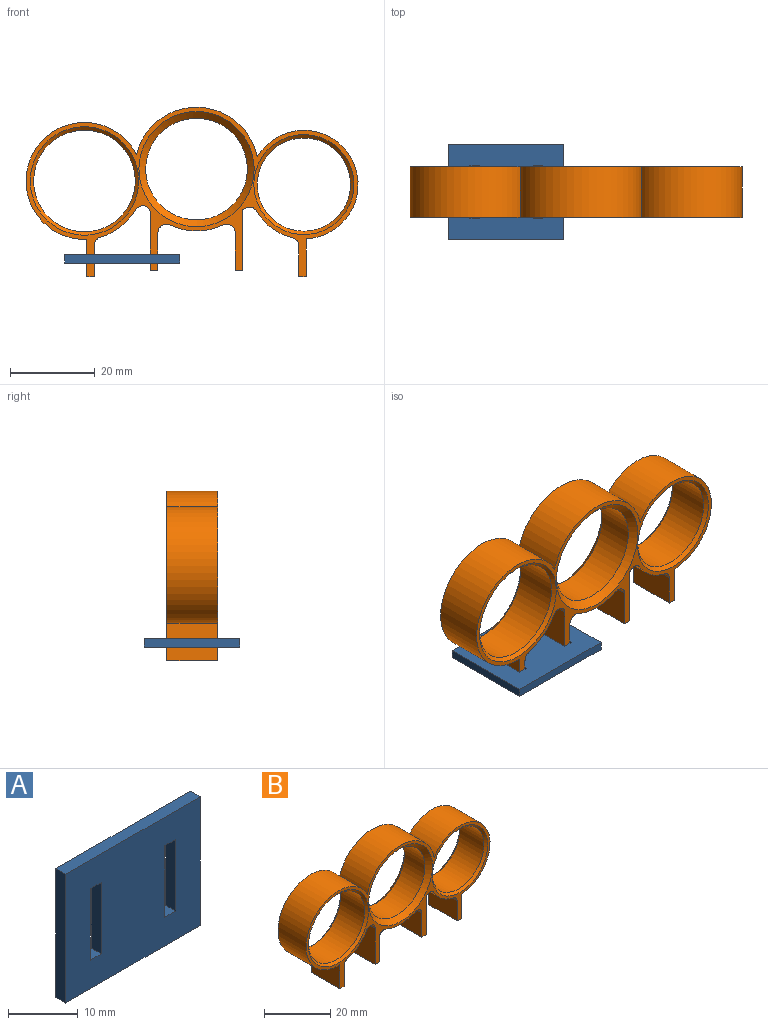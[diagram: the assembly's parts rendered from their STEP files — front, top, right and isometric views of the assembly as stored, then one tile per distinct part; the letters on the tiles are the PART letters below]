
ASSEMBLY  parts=2 mates=1
PART A: 14 faces, bbox 27.2x2x22.5 mm
  f0: plane 27.2x2mm, normal (0,0,1), area 54.4mm2, adj f1,f11,f12,f13
  f1: plane 22.5x2mm, normal (-1,0,0), area 45mm2, adj f0,f2,f12,f13
  f2: plane 27.2x2mm, normal (0,0,-1), area 54.4mm2, adj f1,f11,f12,f13
  f3: plane 12.5x2mm, normal (1,0,0), area 25mm2, adj f4,f9,f12,f13
  f4: plane 2.2x2mm, normal (0,0,-1), area 4.4mm2, adj f3,f5,f12,f13
  f5: plane 12.5x2mm, normal (-1,0,0), area 25mm2, adj f4,f9,f12,f13
  f6: plane 2.2x2mm, normal (0,0,-1), area 4.4mm2, adj f7,f10,f12,f13
  f7: plane 12.5x2mm, normal (-1,0,0), area 25mm2, adj f6,f8,f12,f13
  f8: plane 2.2x2mm, normal (0,0,1), area 4.4mm2, adj f7,f10,f12,f13
  f9: plane 2.2x2mm, normal (0,0,1), area 4.4mm2, adj f3,f5,f12,f13
  f10: plane 12.5x2mm, normal (1,0,0), area 25mm2, adj f6,f8,f12,f13
  f11: plane 22.5x2mm, normal (1,0,0), area 45mm2, adj f0,f2,f12,f13
  f12: plane 27.2x22.5mm, normal (0,-1,0), area 557mm2, adj f0,f1,f2,f3,f4,f5,f6,f7
  f13: plane 27.2x22.5mm, normal (0,1,0), area 557mm2, adj f0,f1,f2,f3,f4,f5,f6,f7
PART B: 37 faces, bbox 78.4x12x40 mm
  f0: cylinder r=12.8mm len=25.59mm, axis (0,1,0), area 635.2mm2, adj f4,f10,f11,f21
  f1: cylinder r=14.6mm len=12.49mm, axis (0,1,0), area 154.9mm2, adj f10,f11,f24,f25
  f2: cylinder r=14.6mm len=12mm, axis (0,1,0), area 1.2mm2, adj f10,f11,f20,f30
  f3: cylinder r=13.8mm len=27.6mm, axis (0,1,0), area 708.5mm2, adj f4,f10,f11,f12
  f4: cylinder r=14.6mm len=28.49mm, axis (0,1,0), area 473.4mm2, adj f0,f3,f10,f11
  f5: cylinder r=13.8mm len=12mm, axis (0,1,0), area 127.9mm2, adj f10,f11,f27,f29
  f6: cylinder r=12mm len=24mm, axis (0,1,0), area 784.1mm2, adj f33,f36
  f7: cylinder r=12mm len=24mm, axis (0,1,0), area 663.5mm2, adj f31,f32
  f8: cylinder r=11mm len=22mm, axis (0,1,0), area 718.8mm2, adj f34,f35
  f9: cylinder r=12.8mm len=12mm, axis (0,1,0), area 128mm2, adj f10,f11,f26,f30
  f10: plane 78.39x40mm, normal (0,-1,0), area 317.2mm2, adj f0,f1,f2,f3,f4,f5,f9,f12
  f11: plane 78.39x40mm, normal (0,1,0), area 317.2mm2, adj f0,f1,f2,f3,f4,f5,f9,f12
  f12: plane 12x8.81mm, normal (-1,0,0), area 105.7mm2, adj f3,f10,f11,f13
  f13: plane 12x1.8mm, normal (0,0,-1), area 21.6mm2, adj f10,f11,f12,f14
  f14: plane 12x7.41mm, normal (1,0,0), area 88.9mm2, adj f10,f11,f13,f29
  f15: plane 12x8.89mm, normal (1,0,0), area 106.7mm2, adj f10,f11,f17,f25
  f16: plane 13.45x12mm, normal (-1,0,0), area 161.4mm2, adj f10,f11,f17,f28
  f17: plane 12x1.8mm, normal (0,0,-1), area 21.6mm2, adj f10,f11,f15,f16
  f18: plane 12x8.89mm, normal (-1,0,0), area 106.7mm2, adj f10,f11,f19,f24
  f19: plane 12x1.8mm, normal (0,0,-1), area 21.6mm2, adj f10,f11,f18,f20
  f20: plane 14.18x12mm, normal (1,0,0), area 170.2mm2, adj f2,f10,f11,f19
  f21: plane 12x8.97mm, normal (1,0,0), area 107.6mm2, adj f0,f10,f11,f23
  f22: plane 12x7.31mm, normal (-1,0,0), area 87.7mm2, adj f10,f11,f23,f26
  f23: plane 12x1.8mm, normal (0,0,-1), area 21.6mm2, adj f10,f11,f21,f22
  f24: cylinder r=2mm len=12mm, axis (0,1,0), area 48.3mm2, adj f1,f10,f11,f18
  f25: cylinder r=2mm len=12mm, axis (0,1,0), area 48.3mm2, adj f1,f10,f11,f15
  f26: cylinder r=2mm len=12mm, axis (0,1,0), area 32.4mm2, adj f9,f10,f11,f22
  f27: cylinder r=2mm len=12mm, axis (0,-1,0), area 44.9mm2, adj f5,f10,f11,f28
  f28: cylinder r=2mm len=12mm, axis (0,1,0), area 15mm2, adj f10,f11,f16,f27
  f29: cylinder r=2mm len=12mm, axis (0,1,0), area 31mm2, adj f5,f10,f11,f14
  f30: cylinder r=2mm len=12mm, axis (0,-1,0), area 45.7mm2, adj f2,f9,f10,f11
  f31: cone r=13.6mm half-angle=45deg, axis (0,1,0), area 182mm2, adj f7,f11
  f32: cone r=12mm half-angle=45deg, axis (0,-1,0), area 182mm2, adj f7,f10
  f33: cone r=12.8mm half-angle=45deg, axis (0,1,0), area 88.1mm2, adj f6,f11
  f34: cone r=11.8mm half-angle=45deg, axis (0,1,0), area 81mm2, adj f8,f11
  f35: cone r=11mm half-angle=45deg, axis (0,-1,0), area 81mm2, adj f8,f10
  f36: cone r=12mm half-angle=45deg, axis (0,-1,0), area 88.1mm2, adj f6,f10
PLACE A rot(axis=(0,-0.71,0.71),180deg) t=(-20.32,-20.47,10.74)mm
PLACE B t=(-2.82,-0.7,0)mm
MATE slider A.f12 <-> B.f17  axis (0,0,1) through (-11.72,-12.9,12.74)mm
